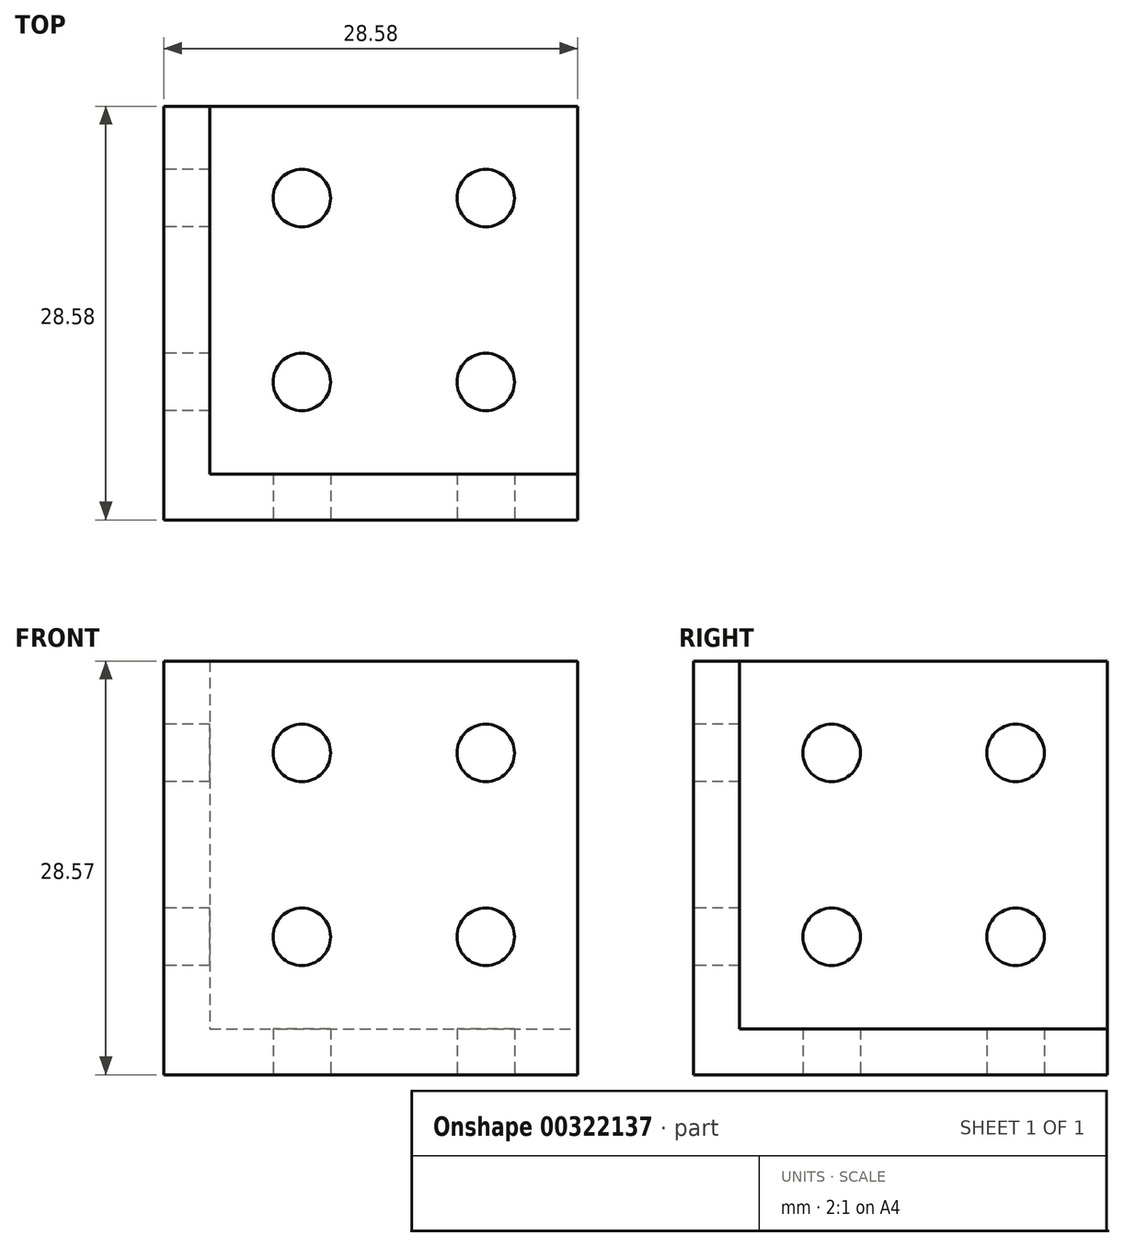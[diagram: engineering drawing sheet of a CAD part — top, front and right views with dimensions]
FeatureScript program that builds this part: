
annotation { "Feature Type Name" : "Feature", "Feature Type Description" : "" }
export const myFeature = defineFeature(function(context is Context, id is Id, definition is map)
    precondition{}
    {
        {
            var Q0;
            Q0=qCreatedBy(makeId("Top.planeOp"),FACE);
            var sketch = newSketch(context, id + "F0", { "sketchPlane" : qUnion([Q0])});
            skLineSegment(sketch, "E0.bottom", {"start": v(-14.29, 12.7) * mm, "end": v(14.29, 12.7) * mm});
            skLineSegment(sketch, "E0.top", {"start": v(-11.11, -12.7) * mm, "end": v(14.29, -12.7) * mm});
            skLineSegment(sketch, "E0.left", {"start": v(-14.29, 12.7) * mm, "end": v(-14.29, -12.7) * mm});
            skLineSegment(sketch, "E0.right", {"start": v(14.29, 12.7) * mm, "end": v(14.29, -12.7) * mm});
            skPoint(sketch, "E0.middle", {"position": v(0, 0) * mm});
            skCircle(sketch, "E1", {"center": v(-4.76, -6.35) * mm, "radius": 1.98 * mm});
            skCircle(sketch, "E2", {"center": v(-4.76, 6.35) * mm, "radius": 1.98 * mm});
            skCircle(sketch, "E3", {"center": v(7.94, 6.35) * mm, "radius": 1.98 * mm});
            skCircle(sketch, "E4", {"center": v(7.94, -6.35) * mm, "radius": 1.98 * mm});
            skLineSegment(sketch, "E5", {"start": v(-11.11, 12.7) * mm, "end": v(-11.11, -12.7) * mm});
            skLineSegment(sketch, "E6.top", {"start": v(-14.29, -15.88) * mm, "end": v(14.29, -15.88) * mm});
            skLineSegment(sketch, "E6.left", {"start": v(-14.29, -12.7) * mm, "end": v(-14.29, -15.88) * mm});
            skLineSegment(sketch, "E6.right", {"start": v(14.29, -12.7) * mm, "end": v(14.29, -15.88) * mm});
            skSolve(sketch);
        }
        {
            var Q0;
            {var subQ0=sQuery(id+"F0.wireOp",EDGE,"E0.left");Q0=makeQuery(id+"F0.imprint","IMPRINT",FACE,{"disambiguationData":[TD([[makeQuery(id+"F0.imprint","IMPRINT",EDGE,{"derivedFrom":subQ0}),1.0]])]});}
            extrude(context, id + "F1", {"entities" : qUnion([Q0]), "depth" : 28.57 * mm});
        }
        {
            var Q0;
            {var subQ0=sQuery(id+"F0.wireOp",EDGE,"E0.right");Q0=makeQuery(id+"F0.imprint","IMPRINT",FACE,{"disambiguationData":[TD([[makeQuery(id+"F0.imprint","IMPRINT",EDGE,{"derivedFrom":subQ0}),-1.0]])]});}
            extrude(context, id + "F2", {"entities" : qUnion([Q0]), "operationType" : NewBodyOperationType.ADD, "depth" : 3.17 * mm});
        }
        {
            var Q0;
            Q0=makeQuery(id+"F1.opExtrude","SWEPT_FACE",FACE,{"disambiguationData":[OSD([sQuery(id+"F0.wireOp",EDGE,"E0.left")])]});
            var sketch = newSketch(context, id + "F3", { "sketchPlane" : qUnion([Q0])});
            skCircle(sketch, "E7", {"center": v(-6.35, 22.23) * mm, "radius": 1.98 * mm});
            skCircle(sketch, "E8", {"center": v(6.35, 22.23) * mm, "radius": 1.98 * mm});
            skCircle(sketch, "E9", {"center": v(6.35, 9.52) * mm, "radius": 1.98 * mm});
            skCircle(sketch, "E10", {"center": v(-6.35, 9.52) * mm, "radius": 1.98 * mm});
            skSolve(sketch);
        }
        {
            var Q0;
            Q0=makeQuery(id+"F1.opExtrude","SWEPT_FACE",FACE,{"disambiguationData":[OSD([sQuery(id+"F0.wireOp",EDGE,"E6.top")])]});
            var sketch = newSketch(context, id + "F4", { "sketchPlane" : qUnion([Q0])});
            skCircle(sketch, "E11", {"center": v(-4.76, 22.23) * mm, "radius": 1.98 * mm});
            skCircle(sketch, "E12", {"center": v(7.94, 22.23) * mm, "radius": 1.98 * mm});
            skCircle(sketch, "E13", {"center": v(7.94, 9.53) * mm, "radius": 1.98 * mm});
            skCircle(sketch, "E14", {"center": v(-4.76, 9.53) * mm, "radius": 1.98 * mm});
            skSolve(sketch);
        }
        {
            var Q0;
            Q0=makeQuery(id+"F3.imprint","IMPRINT",FACE,{"disambiguationData":[TD([[makeQuery(id+"F3.imprint","IMPRINT",EDGE,{"derivedFrom":sQuery(id+"F3.wireOp",EDGE,"E7")}),1.0]])]});
            var Q1;
            Q1=makeQuery(id+"F3.imprint","IMPRINT",FACE,{"disambiguationData":[TD([[makeQuery(id+"F3.imprint","IMPRINT",EDGE,{"derivedFrom":sQuery(id+"F3.wireOp",EDGE,"E8")}),1.0]])]});
            var Q2;
            Q2=makeQuery(id+"F3.imprint","IMPRINT",FACE,{"disambiguationData":[TD([[makeQuery(id+"F3.imprint","IMPRINT",EDGE,{"derivedFrom":sQuery(id+"F3.wireOp",EDGE,"E9")}),1.0]])]});
            var Q3;
            Q3=makeQuery(id+"F3.imprint","IMPRINT",FACE,{"disambiguationData":[TD([[makeQuery(id+"F3.imprint","IMPRINT",EDGE,{"derivedFrom":sQuery(id+"F3.wireOp",EDGE,"E10")}),1.0]])]});
            extrude(context, id + "F5", {"entities" : qUnion([Q0, Q1, Q2, Q3]), "operationType" : NewBodyOperationType.REMOVE, "oppositeDirection" : true, "depth" : 25.4 * mm});
        }
        {
            var Q0;
            Q0=makeQuery(id+"F4.imprint","IMPRINT",FACE,{"disambiguationData":[TD([[makeQuery(id+"F4.imprint","IMPRINT",EDGE,{"derivedFrom":sQuery(id+"F4.wireOp",EDGE,"E12")}),1.0]])]});
            var Q1;
            Q1=makeQuery(id+"F4.imprint","IMPRINT",FACE,{"disambiguationData":[TD([[makeQuery(id+"F4.imprint","IMPRINT",EDGE,{"derivedFrom":sQuery(id+"F4.wireOp",EDGE,"E13")}),1.0]])]});
            var Q2;
            Q2=makeQuery(id+"F4.imprint","IMPRINT",FACE,{"disambiguationData":[TD([[makeQuery(id+"F4.imprint","IMPRINT",EDGE,{"derivedFrom":sQuery(id+"F4.wireOp",EDGE,"E14")}),1.0]])]});
            var Q3;
            Q3=makeQuery(id+"F4.imprint","IMPRINT",FACE,{"disambiguationData":[TD([[makeQuery(id+"F4.imprint","IMPRINT",EDGE,{"derivedFrom":sQuery(id+"F4.wireOp",EDGE,"E11")}),1.0]])]});
            extrude(context, id + "F6", {"entities" : qUnion([Q0, Q1, Q2, Q3]), "operationType" : NewBodyOperationType.REMOVE, "oppositeDirection" : true, "depth" : 25.4 * mm});
        }
    });
